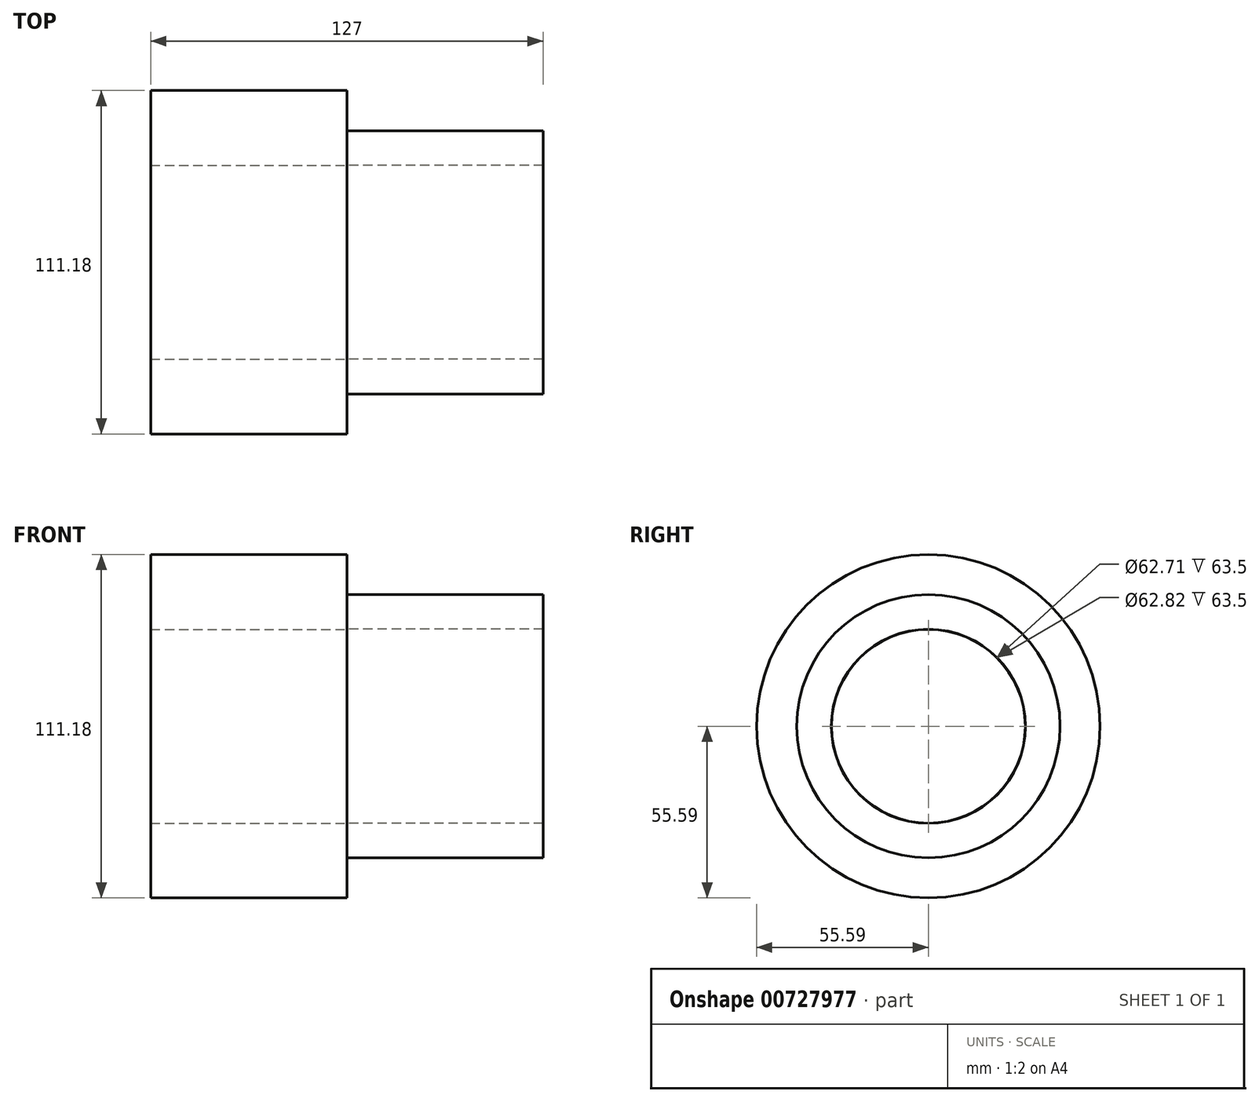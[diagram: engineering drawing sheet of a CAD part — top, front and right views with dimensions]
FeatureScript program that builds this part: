
annotation { "Feature Type Name" : "Feature", "Feature Type Description" : "" }
export const myFeature = defineFeature(function(context is Context, id is Id, definition is map)
    precondition{}
    {
        {
            var Q0;
            Q0=qCreatedBy(makeId("Right.planeOp"),FACE);
            var sketch = newSketch(context, id + "F0", { "sketchPlane" : qUnion([Q0])});
            skCircle(sketch, "E0", {"center": v(0, 0) * mm, "radius": 55.59 * mm});
            skSolve(sketch);
        }
        {
            var Q0;
            Q0=makeQuery(id+"F0.imprint","IMPRINT",FACE,{"disambiguationData":[TD([[makeQuery(id+"F0.imprint","IMPRINT",EDGE,{"derivedFrom":sQuery(id+"F0.wireOp",EDGE,"E0")}),1.0]])]});
            extrude(context, id + "F1", {"entities" : qUnion([Q0]), "depth" : 63.5 * mm, "offsetDistance" : 25.4 * mm});
        }
        {
            var Q0;
            Q0=makeQuery(id+"F1.opExtrude","CAP_FACE",FACE,{"disambiguationData":[OSD([sQuery(id+"F0.wireOp",EDGE,"E0")])],"isStart":false});
            var sketch = newSketch(context, id + "F2", { "sketchPlane" : qUnion([Q0])});
            skCircle(sketch, "E1", {"center": v(0, 0) * mm, "radius": 31.36 * mm});
            skSolve(sketch);
        }
        {
            var Q0;
            Q0=makeQuery(id+"F2.imprint","IMPRINT",FACE,{"disambiguationData":[TD([[makeQuery(id+"F2.imprint","IMPRINT",EDGE,{"derivedFrom":sQuery(id+"F2.wireOp",EDGE,"E1")}),1.0]])]});
            extrude(context, id + "F3", {"entities" : qUnion([Q0]), "operationType" : NewBodyOperationType.REMOVE, "oppositeDirection" : true, "depth" : 63.5 * mm, "offsetDistance" : 25.4 * mm});
        }
        {
            var Q0;
            Q0=makeQuery(id+"F1.opExtrude","CAP_FACE",FACE,{"disambiguationData":[OSD([sQuery(id+"F0.wireOp",EDGE,"E0")])],"isStart":false});
            var sketch = newSketch(context, id + "F4", { "sketchPlane" : qUnion([Q0])});
            skCircle(sketch, "E2", {"center": v(0, 0) * mm, "radius": 42.62 * mm});
            skSolve(sketch);
        }
        {
            var Q0;
            Q0 = qSketchRegion(id + "F4", true);
            extrude(context, id + "F5", {"entities" : qUnion([Q0]), "operationType" : NewBodyOperationType.ADD, "depth" : 63.5 * mm, "offsetDistance" : 25.4 * mm});
        }
        {
            var Q0;
            Q0=makeQuery(id+"F5.opExtrude","CAP_FACE",FACE,{"disambiguationData":[OSD([sQuery(id+"F4.wireOp",EDGE,"E2")])],"isStart":true});
            var sketch = newSketch(context, id + "F6", { "sketchPlane" : qUnion([Q0])});
            skCircle(sketch, "E3", {"center": v(0, 0) * mm, "radius": 31.4 * mm});
            skSolve(sketch);
        }
        {
            var Q0;
            Q0 = qSketchRegion(id + "F6", true);
            extrude(context, id + "F7", {"entities" : qUnion([Q0]), "operationType" : NewBodyOperationType.REMOVE, "oppositeDirection" : true, "depth" : 63.5 * mm, "offsetDistance" : 25.4 * mm});
        }
    });
